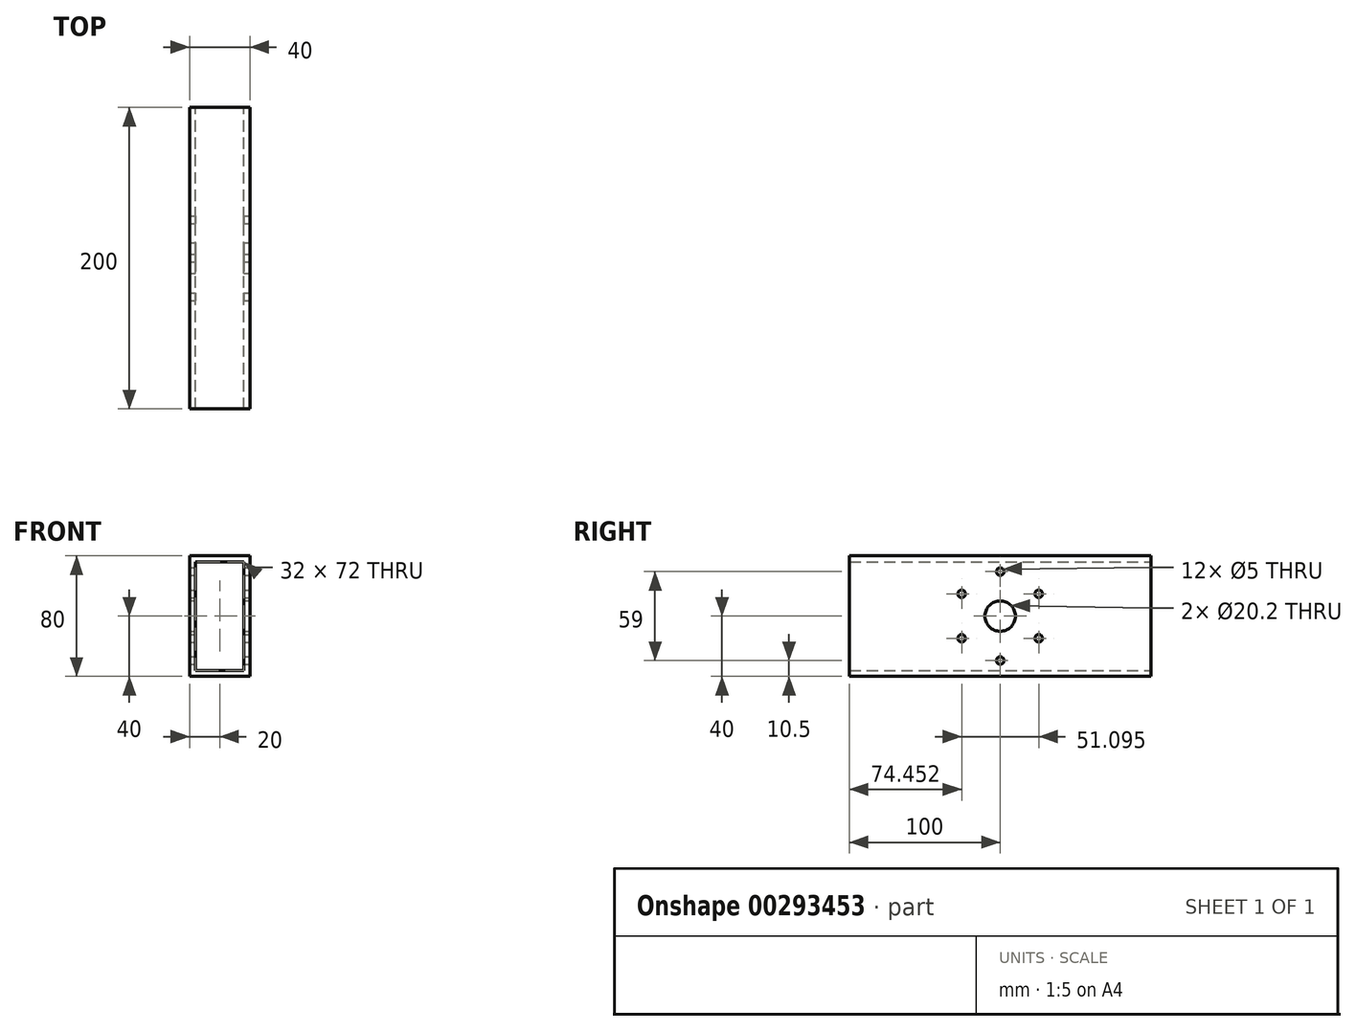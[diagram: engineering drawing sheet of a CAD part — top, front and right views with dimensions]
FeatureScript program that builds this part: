
annotation { "Feature Type Name" : "Feature", "Feature Type Description" : "" }
export const myFeature = defineFeature(function(context is Context, id is Id, definition is map)
    precondition{}
    {
        {
            var Q0;
            Q0=qCreatedBy(makeId("Front.planeOp"),FACE);
            var sketch = newSketch(context, id + "F0", { "sketchPlane" : qUnion([Q0])});
            skLineSegment(sketch, "E0.bottom", {"start": v(-20, 40) * mm, "end": v(20, 40) * mm});
            skLineSegment(sketch, "E0.top", {"start": v(-20, -40) * mm, "end": v(20, -40) * mm});
            skLineSegment(sketch, "E0.left", {"start": v(-20, 40) * mm, "end": v(-20, -40) * mm});
            skLineSegment(sketch, "E0.right", {"start": v(20, 40) * mm, "end": v(20, -40) * mm});
            skPoint(sketch, "E0.middle", {"position": v(0, 0) * mm});
            skLineSegment(sketch, "E1.0", {"start": v(-16, 36) * mm, "end": v(16, 36) * mm});
            skLineSegment(sketch, "E1.1", {"start": v(-16, 36) * mm, "end": v(-16, -36) * mm});
            skLineSegment(sketch, "E1.2", {"start": v(-16, -36) * mm, "end": v(16, -36) * mm});
            skLineSegment(sketch, "E1.3", {"start": v(16, 36) * mm, "end": v(16, -36) * mm});
            skSolve(sketch);
        }
        {
            var Q0;
            Q0=makeQuery(id+"F0.imprint","IMPRINT",FACE,{"disambiguationData":[TD([[makeQuery(id+"F0.imprint","IMPRINT",EDGE,{"derivedFrom":sQuery(id+"F0.wireOp",EDGE,"E0.bottom")}),-1.0]])]});
            extrude(context, id + "F1", {"entities" : qUnion([Q0]), "depth" : 200 * mm});
        }
        {
            var Q0;
            Q0=makeQuery(id+"F1.opExtrude","SWEPT_FACE",FACE,{"disambiguationData":[OSD([sQuery(id+"F0.wireOp",EDGE,"E0.right")])]});
            var sketch = newSketch(context, id + "F2", { "sketchPlane" : qUnion([Q0])});
            skCircle(sketch, "E2", {"center": v(-100, 0) * mm, "radius": 10.1 * mm});
            skSolve(sketch);
        }
        {
            var Q0;
            Q0=makeQuery(id+"F2.imprint","IMPRINT",FACE,{"disambiguationData":[TD([[makeQuery(id+"F2.imprint","IMPRINT",EDGE,{"derivedFrom":sQuery(id+"F2.wireOp",EDGE,"E2")}),1.0]])]});
            extrude(context, id + "F3", {"entities" : qUnion([Q0]), "operationType" : NewBodyOperationType.REMOVE, "endBound" : BoundingType.THROUGH_ALL, "oppositeDirection" : true, "depth" : 25 * mm});
        }
        {
            var Q0;
            Q0=makeQuery(id+"F1.opExtrude","SWEPT_FACE",FACE,{"disambiguationData":[OSD([sQuery(id+"F0.wireOp",EDGE,"E0.right")])]});
            var sketch = newSketch(context, id + "F4", { "sketchPlane" : qUnion([Q0])});
            skLineSegment(sketch, "E3", {"start": v(-100, 0) * mm, "end": v(-100, 48.03) * mm, "construction": true});
            skPoint(sketch, "E3.endSnap0", {"position": v(-100, 40) * mm});
            skCircle(sketch, "E4", {"center": v(-100, 29.5) * mm, "radius": 2.5 * mm});
            skCircle(sketch, "E5.1.0", {"center": v(-125.55, 14.75) * mm, "radius": 2.5 * mm});
            skCircle(sketch, "E5.2.0", {"center": v(-125.55, -14.75) * mm, "radius": 2.5 * mm});
            skCircle(sketch, "E5.3.0", {"center": v(-100, -29.5) * mm, "radius": 2.5 * mm});
            skCircle(sketch, "E5.4.0", {"center": v(-74.45, -14.75) * mm, "radius": 2.5 * mm});
            skCircle(sketch, "E5.5.0", {"center": v(-74.45, 14.75) * mm, "radius": 2.5 * mm});
            skPoint(sketch, "E5.center", {"position": v(-100, 0) * mm});
            skSolve(sketch);
        }
        {
            var Q0;
            Q0=makeQuery(id+"F4.imprint","IMPRINT",FACE,{"disambiguationData":[TD([[makeQuery(id+"F4.imprint","IMPRINT",EDGE,{"derivedFrom":sQuery(id+"F4.wireOp",EDGE,"E5.2.0")}),1.0]])]});
            var Q1;
            Q1=makeQuery(id+"F4.imprint","IMPRINT",FACE,{"disambiguationData":[TD([[makeQuery(id+"F4.imprint","IMPRINT",EDGE,{"derivedFrom":sQuery(id+"F4.wireOp",EDGE,"E5.1.0")}),1.0]])]});
            var Q2;
            Q2=makeQuery(id+"F4.imprint","IMPRINT",FACE,{"disambiguationData":[TD([[makeQuery(id+"F4.imprint","IMPRINT",EDGE,{"derivedFrom":sQuery(id+"F4.wireOp",EDGE,"E4")}),1.0]])]});
            var Q3;
            Q3=makeQuery(id+"F4.imprint","IMPRINT",FACE,{"disambiguationData":[TD([[makeQuery(id+"F4.imprint","IMPRINT",EDGE,{"derivedFrom":sQuery(id+"F4.wireOp",EDGE,"E5.5.0")}),1.0]])]});
            var Q4;
            Q4=makeQuery(id+"F4.imprint","IMPRINT",FACE,{"disambiguationData":[TD([[makeQuery(id+"F4.imprint","IMPRINT",EDGE,{"derivedFrom":sQuery(id+"F4.wireOp",EDGE,"E5.4.0")}),1.0]])]});
            var Q5;
            Q5=makeQuery(id+"F4.imprint","IMPRINT",FACE,{"disambiguationData":[TD([[makeQuery(id+"F4.imprint","IMPRINT",EDGE,{"derivedFrom":sQuery(id+"F4.wireOp",EDGE,"E5.3.0")}),1.0]])]});
            extrude(context, id + "F5", {"entities" : qUnion([Q0, Q1, Q2, Q3, Q4, Q5]), "operationType" : NewBodyOperationType.REMOVE, "endBound" : BoundingType.THROUGH_ALL, "oppositeDirection" : true, "depth" : 25 * mm});
        }
    });
